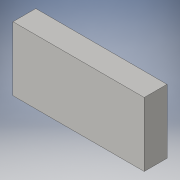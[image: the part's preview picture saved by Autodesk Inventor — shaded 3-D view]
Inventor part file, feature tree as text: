
AUTODESK INVENTOR PART (.ipt)
format: ipt  version: 2016 (Build 200138000, 138)  size: 81,408 bytes
history: native  units: in
note: dims shown in document units (in); Inventor stores cm internally (conversion verified against a paired STEP export)
features: extrude x1, sketch x1
ambient origin geometry x8: Origin, YZ Plane, XZ Plane, XY Plane, X Axis, Y Axis, Z Axis, Center Point
bodies: Solid1 (feature_tree)
feature tree (2):
  extrude  "Extrusion1"  Depth=2.728in
  sketch  "Sketch1"  dims[d0=1.332in d1=2.728in d2=0.474in d3=0.0in]
